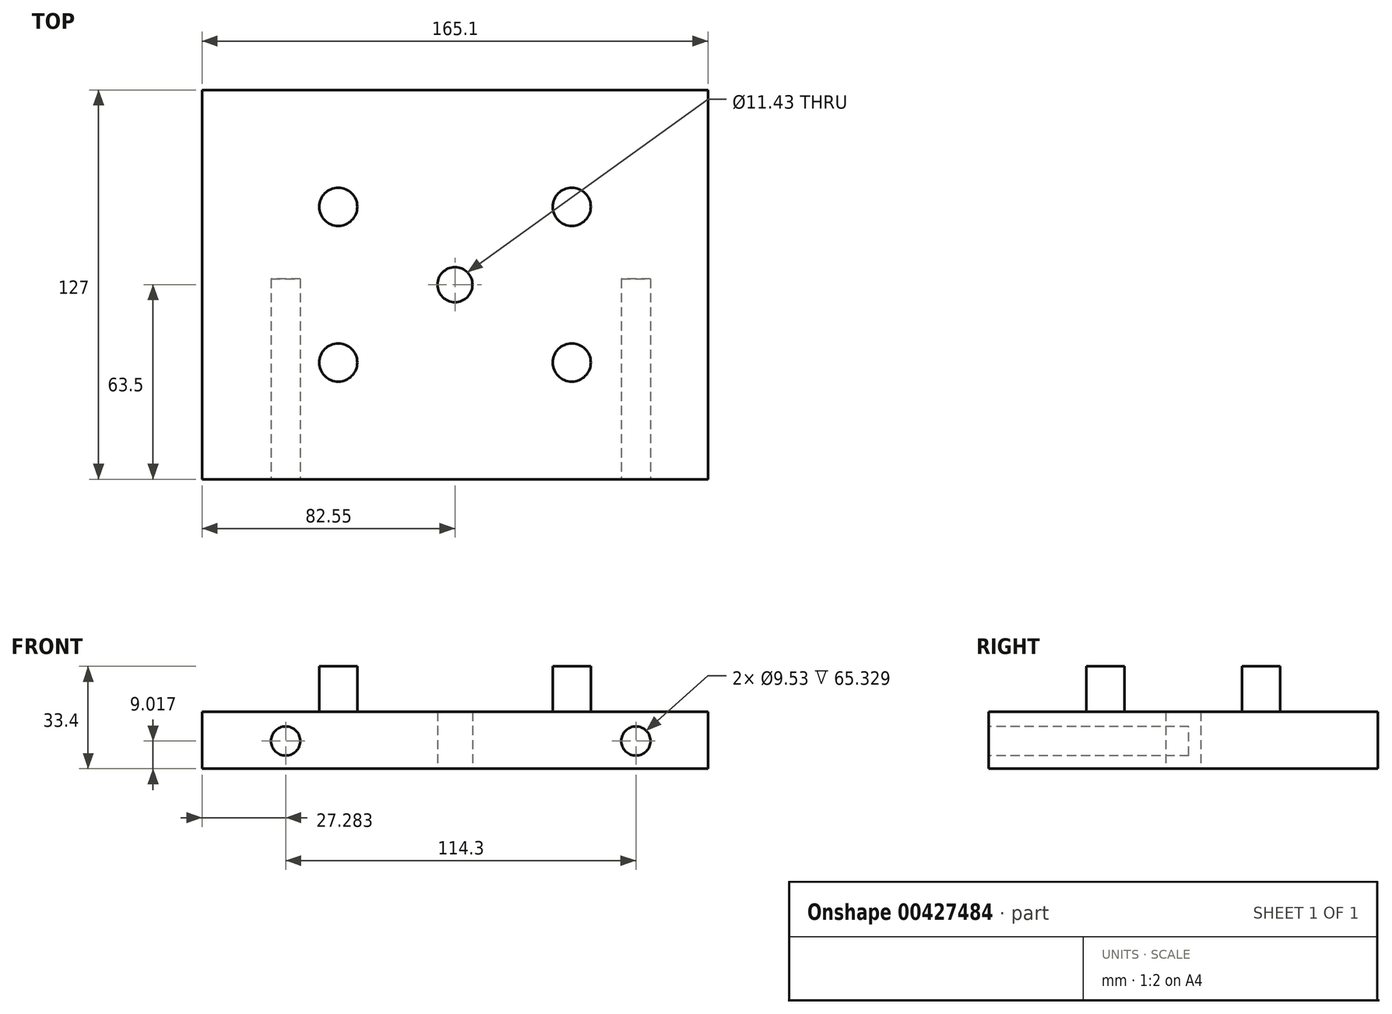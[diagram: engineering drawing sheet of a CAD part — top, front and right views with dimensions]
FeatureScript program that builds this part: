
annotation { "Feature Type Name" : "Feature", "Feature Type Description" : "" }
export const myFeature = defineFeature(function(context is Context, id is Id, definition is map)
    precondition{}
    {
        {
            var Q0;
            Q0=qCreatedBy(makeId("Top.planeOp"),FACE);
            var sketch = newSketch(context, id + "F0", { "sketchPlane" : qUnion([Q0])});
            skLineSegment(sketch, "E0.bottom", {"start": v(0, 0) * mm, "end": v(165.1, 0) * mm});
            skLineSegment(sketch, "E0.top", {"start": v(0, 127) * mm, "end": v(165.1, 127) * mm});
            skLineSegment(sketch, "E0.left", {"start": v(0, 0) * mm, "end": v(0, 127) * mm});
            skLineSegment(sketch, "E0.right", {"start": v(165.1, 0) * mm, "end": v(165.1, 127) * mm});
            skCircle(sketch, "E1", {"center": v(82.55, 63.5) * mm, "radius": 5.72 * mm});
            skSolve(sketch);
        }
        {
            var Q0;
            Q0 = qSketchRegion(id + "F0", true);
            extrude(context, id + "F1", {"entities" : qUnion([Q0]), "depth" : 18.54 * mm});
        }
        {
            var Q0;
            Q0=makeQuery(id+"F1.opExtrude","CAP_FACE",FACE,{"disambiguationData":[OSD([sQuery(id+"F0.wireOp",EDGE,"E0.bottom"),sQuery(id+"F0.wireOp",EDGE,"E0.top"),sQuery(id+"F0.wireOp",EDGE,"E0.left"),sQuery(id+"F0.wireOp",EDGE,"E0.right"),sQuery(id+"F0.wireOp",EDGE,"E1")])],"isStart":false});
            var sketch = newSketch(context, id + "F2", { "sketchPlane" : qUnion([Q0])});
            skCircle(sketch, "E2", {"center": v(44.45, 88.9) * mm, "radius": 6.22 * mm});
            skCircle(sketch, "E3", {"center": v(120.65, 88.9) * mm, "radius": 6.22 * mm});
            skCircle(sketch, "E4", {"center": v(120.65, 38.1) * mm, "radius": 6.22 * mm});
            skCircle(sketch, "E5", {"center": v(44.45, 38.1) * mm, "radius": 6.22 * mm});
            skSolve(sketch);
        }
        {
            var Q0;
            Q0 = qSketchRegion(id + "F2", true);
            extrude(context, id + "F3", {"entities" : qUnion([Q0]), "operationType" : NewBodyOperationType.ADD, "depth" : 14.86 * mm});
        }
        {
            var Q0;
            Q0=makeQuery(id+"F1.opExtrude","SWEPT_FACE",FACE,{"disambiguationData":[OSD([sQuery(id+"F0.wireOp",EDGE,"E0.bottom")])]});
            var sketch = newSketch(context, id + "F4", { "sketchPlane" : qUnion([Q0])});
            skCircle(sketch, "E6", {"center": v(27.28, 9.02) * mm, "radius": 4.76 * mm});
            skCircle(sketch, "E7", {"center": v(141.58, 9.02) * mm, "radius": 4.76 * mm});
            skSolve(sketch);
        }
        {
            var Q0;
            Q0 = qSketchRegion(id + "F4", true);
            extrude(context, id + "F5", {"entities" : qUnion([Q0]), "operationType" : NewBodyOperationType.REMOVE, "oppositeDirection" : true, "depth" : 65.33 * mm});
        }
    });
